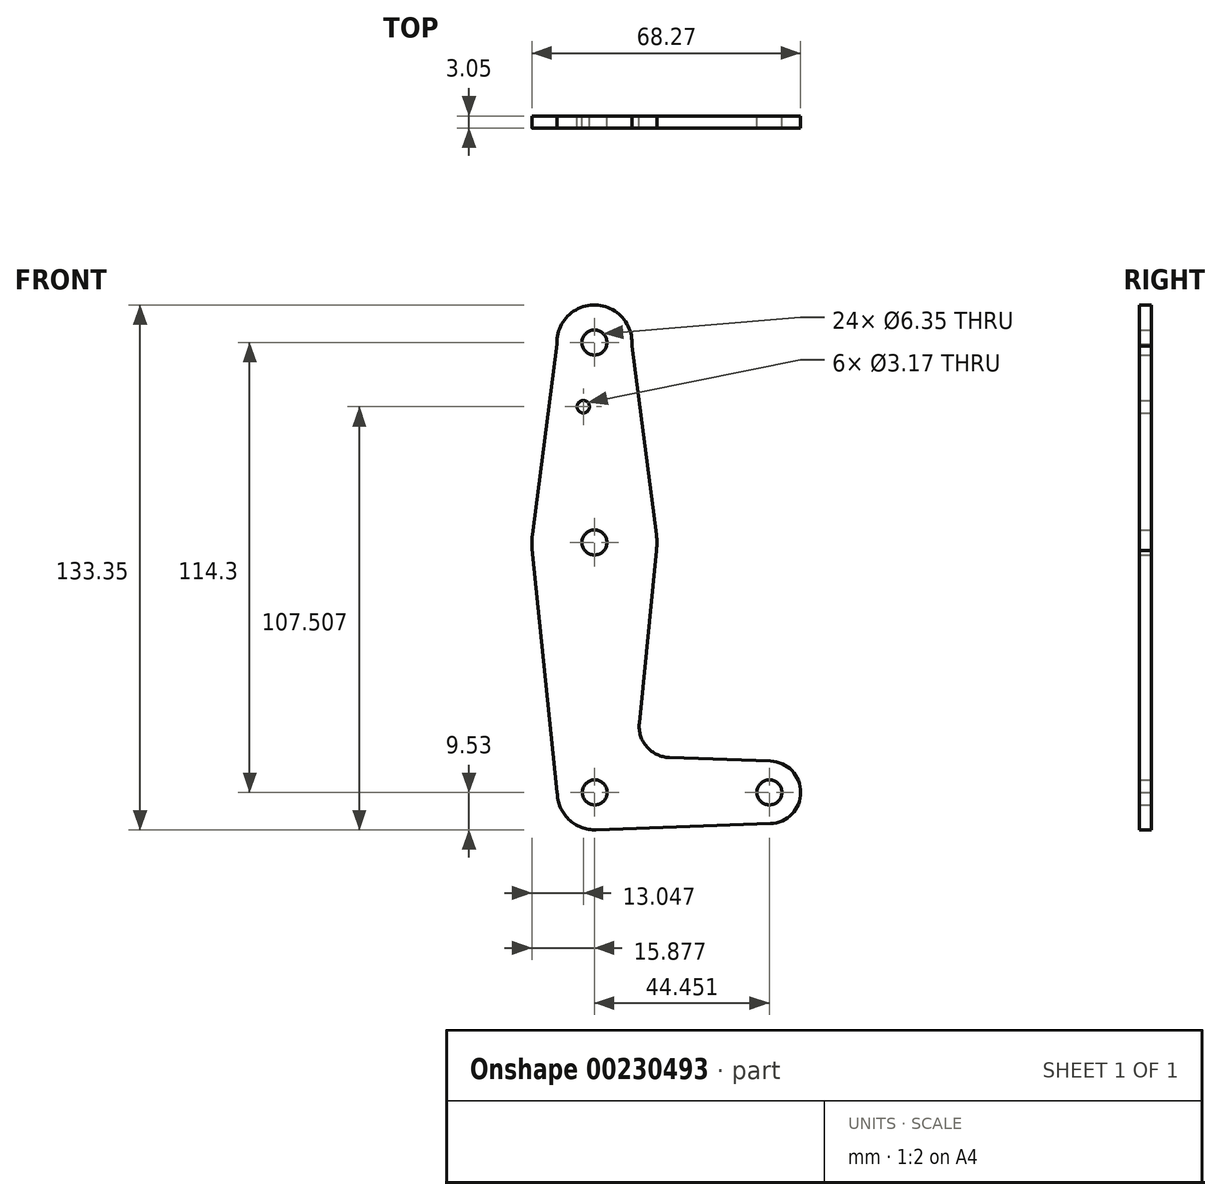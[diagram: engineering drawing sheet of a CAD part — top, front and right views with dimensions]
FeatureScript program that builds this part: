
annotation { "Feature Type Name" : "Feature", "Feature Type Description" : "" }
export const myFeature = defineFeature(function(context is Context, id is Id, definition is map)
    precondition{}
    {
        {
            var Q0;
            Q0=qCreatedBy(makeId("Front.planeOp"),FACE);
            var sketch = newSketch(context, id + "F0", { "sketchPlane" : qUnion([Q0])});
            skLineSegment(sketch, "E0", {"start": v(-85.28, 0) * mm, "end": v(-40.83, 0) * mm});
            skCircle(sketch, "E1", {"center": v(-85.27, 114.3) * mm, "radius": 9.53 * mm});
            skCircle(sketch, "E2", {"center": v(-85.28, 63.5) * mm, "radius": 15.88 * mm});
            skCircle(sketch, "E3", {"center": v(-40.83, 0) * mm, "radius": 7.94 * mm});
            skLineSegment(sketch, "E4", {"start": v(-85.2, 0) * mm, "end": v(-85.28, 0) * mm});
            skLineSegment(sketch, "E5", {"start": v(-85.27, 114.3) * mm, "end": v(-85.2, 0) * mm});
            skLineSegment(sketch, "E6", {"start": v(-94.8, 113.93) * mm, "end": v(-101.03, 65.53) * mm});
            skCircle(sketch, "E7", {"center": v(-85.2, 0) * mm, "radius": 9.53 * mm});
            skLineSegment(sketch, "E8", {"start": v(-94.73, 0) * mm, "end": v(-101.08, 61.88) * mm});
            skLineSegment(sketch, "E9", {"start": v(-75.79, 113.41) * mm, "end": v(-69.54, 65.56) * mm});
            skLineSegment(sketch, "E10", {"start": v(-69.54, 61.44) * mm, "end": v(-73.89, 17.58) * mm});
            skLineSegment(sketch, "E11", {"start": v(-66.26, 8.85) * mm, "end": v(-40.55, 7.93) * mm});
            skLineSegment(sketch, "E12", {"start": v(-84.86, -9.52) * mm, "end": v(-40.55, -7.93) * mm});
            skCircle(sketch, "E13", {"center": v(-85.27, 114.3) * mm, "radius": 3.18 * mm});
            skCircle(sketch, "E14", {"center": v(-85.28, 63.5) * mm, "radius": 3.18 * mm});
            skCircle(sketch, "E15", {"center": v(-85.2, 0) * mm, "radius": 3.18 * mm});
            skCircle(sketch, "E16", {"center": v(-40.83, 0) * mm, "radius": 3.18 * mm});
            skArc(sketch, "E17.filletArc", {"start": v(-73.89, 17.58) * mm, "mid": v(-71.96, 11.56) * mm, "end": v(-66.26, 8.85) * mm});
            skCircle(sketch, "E18", {"center": v(-88.11, 97.98) * mm, "radius": 1.59 * mm});
            skSolve(sketch);
        }
        {
            var Q0;
            Q0 = qSketchRegion(id + "F0", true);
            var Q1;
            {var subQ0=sQuery(id+"F0.wireOp",EDGE,"E15");var subQ1=sQuery(id+"F0.wireOp",EDGE,"E0");var subQ2=makeQuery(id+"F0.imprint","INTERSECT",VERTEX,{"derivedFrom":[subQ1,subQ0]});Q1=makeQuery(id+"F0.imprint","IMPRINT",FACE,{"disambiguationData":[TD([[makeQuery(id+"F0.imprint","IMPRINT",EDGE,{"disambiguationData":[TD([[subQ2,-1.0]])],"derivedFrom":subQ1}),1.0]])]});}
            extrude(context, id + "F1", {"entities" : qUnion([Q0, Q1]), "depth" : 3.05 * mm});
        }
    });
